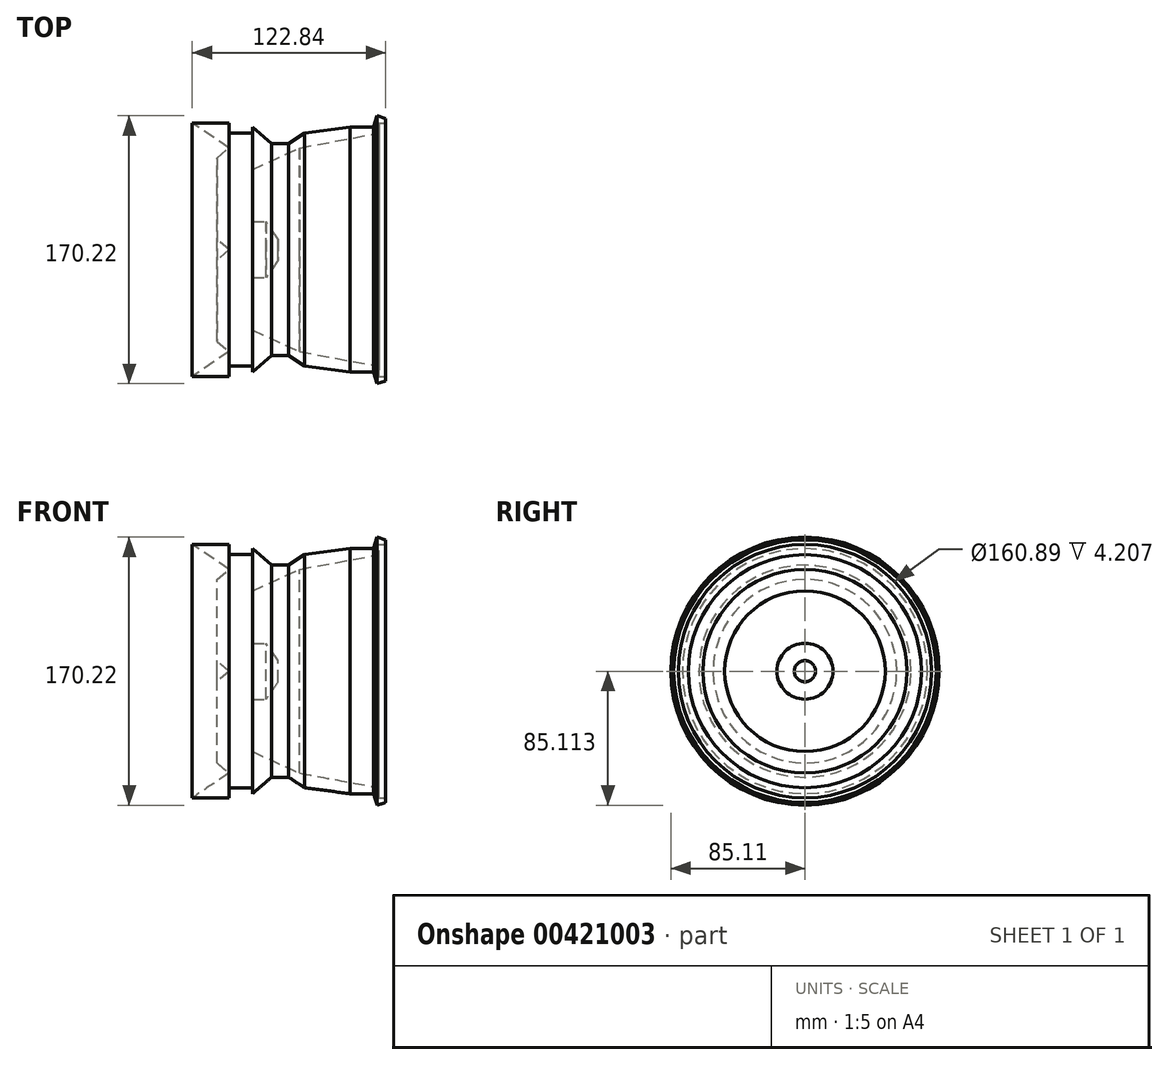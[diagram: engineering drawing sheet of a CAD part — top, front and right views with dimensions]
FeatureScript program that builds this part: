
annotation { "Feature Type Name" : "Feature", "Feature Type Description" : "" }
export const myFeature = defineFeature(function(context is Context, id is Id, definition is map)
    precondition{}
    {
        {
            var Q0;
            Q0=qCreatedBy(makeId("Front.planeOp"),FACE);
            var sketch = newSketch(context, id + "F0", { "sketchPlane" : qUnion([Q0])});
            skLineSegment(sketch, "E0", {"start": v(-50.13, 48.53) * mm, "end": v(-44.89, 48.53) * mm});
            skLineSegment(sketch, "E1", {"start": v(-44.89, 48.53) * mm, "end": v(-44.89, 42.12) * mm});
            skLineSegment(sketch, "E2", {"start": v(-44.89, 42.12) * mm, "end": v(-30.02, 42.12) * mm});
            skLineSegment(sketch, "E3", {"start": v(-30.02, 42.12) * mm, "end": v(-30.02, 45.9) * mm});
            skLineSegment(sketch, "E4", {"start": v(-30.02, 45.9) * mm, "end": v(-17.78, 35.41) * mm});
            skLineSegment(sketch, "E5", {"start": v(-17.78, 35.41) * mm, "end": v(-7, 35.41) * mm});
            skLineSegment(sketch, "E6", {"start": v(-7, 35.41) * mm, "end": v(3.2, 42.12) * mm});
            skLineSegment(sketch, "E7", {"start": v(3.2, 42.12) * mm, "end": v(32.06, 45.9) * mm});
            skLineSegment(sketch, "E8", {"start": v(32.06, 45.9) * mm, "end": v(46.93, 45.9) * mm});
            skLineSegment(sketch, "E9", {"start": v(46.93, 45.9) * mm, "end": v(49.26, 53.2) * mm});
            skLineSegment(sketch, "E10", {"start": v(49.26, 53.2) * mm, "end": v(54.63, 51.48) * mm});
            skLineSegment(sketch, "E11", {"start": v(54.63, 51.48) * mm, "end": v(54.63, 48.53) * mm});
            skLineSegment(sketch, "E12", {"start": v(54.63, 48.53) * mm, "end": v(50.43, 48.53) * mm});
            skLineSegment(sketch, "E13", {"start": v(50.43, 48.53) * mm, "end": v(50.43, 42.12) * mm});
            skLineSegment(sketch, "E14", {"start": v(50.43, 42.12) * mm, "end": v(0, 32.8) * mm});
            skLineSegment(sketch, "E15", {"start": v(0, 32.8) * mm, "end": v(-30.02, 19.1) * mm});
            skLineSegment(sketch, "E16", {"start": v(-30.02, 19.1) * mm, "end": v(-30.02, -14.14) * mm});
            skLineSegment(sketch, "E17", {"start": v(-30.02, -14.14) * mm, "end": v(-21.28, -14.14) * mm});
            skLineSegment(sketch, "E18", {"start": v(-21.28, -14.14) * mm, "end": v(-13.7, -25.21) * mm});
            skLineSegment(sketch, "E19", {"start": v(-13.7, -25.21) * mm, "end": v(-13.7, -31.92) * mm});
            skLineSegment(sketch, "E20", {"start": v(-13.7, -31.92) * mm, "end": v(-44.89, -31.92) * mm});
            skLineSegment(sketch, "E21", {"start": v(-44.89, -31.92) * mm, "end": v(-52.47, -25.21) * mm});
            skLineSegment(sketch, "E22", {"start": v(-52.47, -25.21) * mm, "end": v(-52.47, 26.38) * mm});
            skLineSegment(sketch, "E23", {"start": v(-52.47, 26.38) * mm, "end": v(-44.89, 32.8) * mm});
            skLineSegment(sketch, "E24", {"start": v(-44.89, 32.8) * mm, "end": v(-68.2, 48.53) * mm});
            skLineSegment(sketch, "E25", {"start": v(-68.2, 48.53) * mm, "end": v(-50.13, 48.53) * mm});
            skSolve(sketch);
        }
        {
            var Q0;
            Q0=makeQuery(id+"F0.imprint","IMPRINT",FACE,{"disambiguationData":[TD([[makeQuery(id+"F0.imprint","IMPRINT",EDGE,{"derivedFrom":sQuery(id+"F0.wireOp",EDGE,"E0")}),-1.0]])]});
            var Q1;
            Q1=sQuery(id+"F0.wireOp",EDGE,"E20");
            revolve(context, id + "F1", {"entities" : qUnion([Q0]), "axis" : qUnion([Q1]), "revolveType" : RevolveType.FULL});
        }
    });
